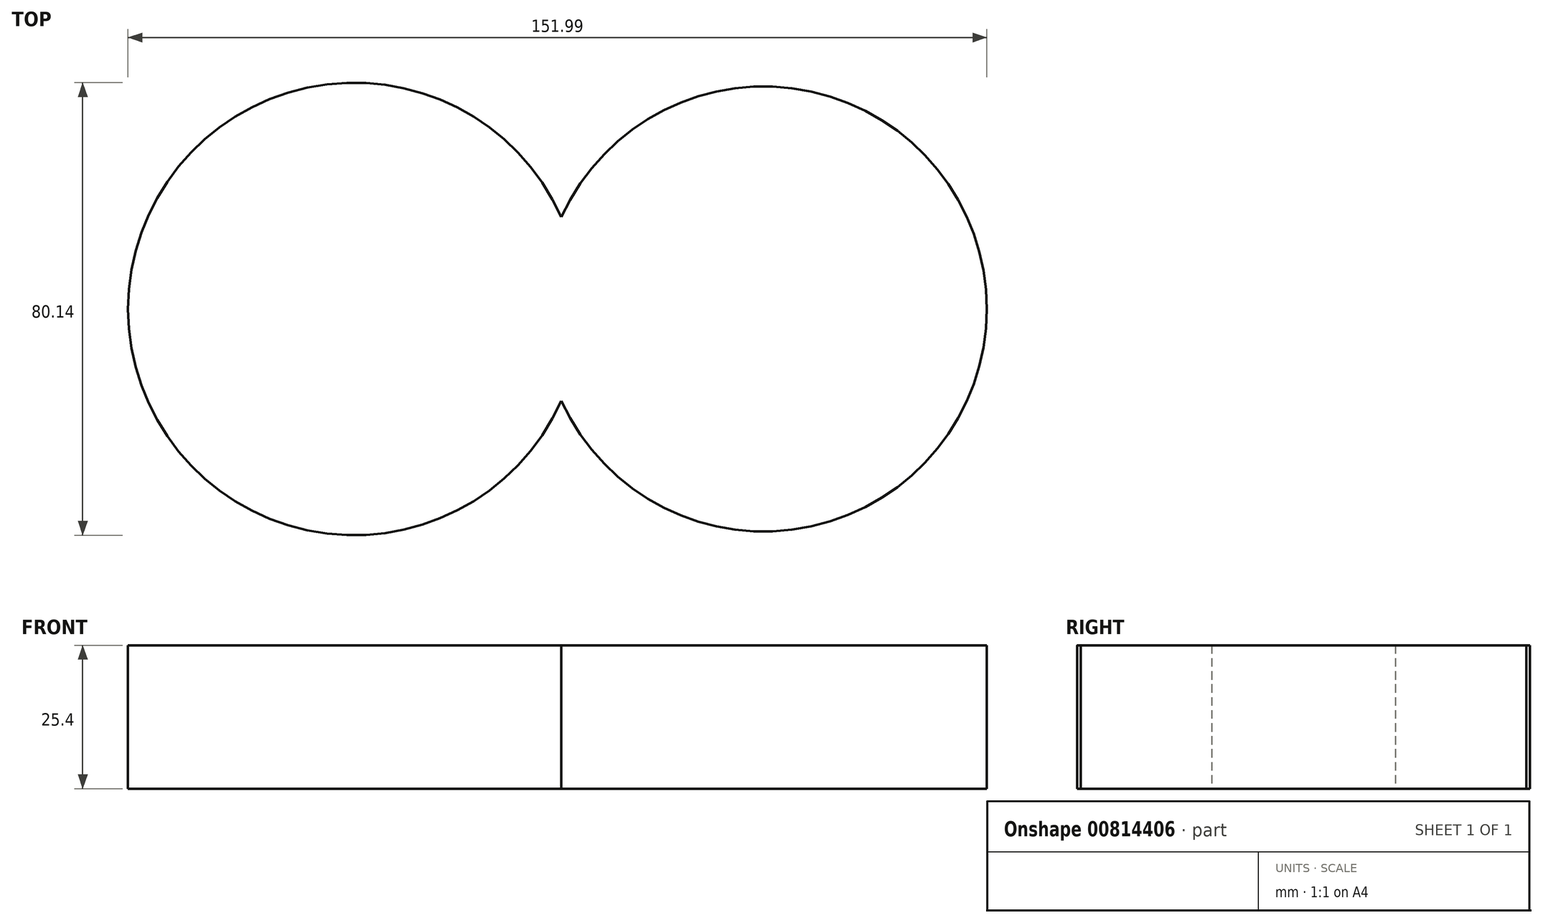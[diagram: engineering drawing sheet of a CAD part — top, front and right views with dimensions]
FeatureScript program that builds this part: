
annotation { "Feature Type Name" : "Feature", "Feature Type Description" : "" }
export const myFeature = defineFeature(function(context is Context, id is Id, definition is map)
    precondition{}
    {
        {
            var Q0;
            Q0=qCreatedBy(makeId("Top.planeOp"),FACE);
            var sketch = newSketch(context, id + "F0", { "sketchPlane" : qUnion([Q0])});
            skArc(sketch, "E0", {"start": v(0, 0) * mm, "mid": v(75.31, 16.26) * mm, "end": v(0, 32.52) * mm});
            skArc(sketch, "E1", {"start": v(0, 32.52) * mm, "mid": v(-76.68, 16.26) * mm, "end": v(0, 0) * mm});
            skSolve(sketch);
        }
        {
            var Q0;
            Q0=makeQuery(id+"F0.imprint","IMPRINT",FACE,{"disambiguationData":[TD([[makeQuery(id+"F0.imprint","IMPRINT",EDGE,{"derivedFrom":sQuery(id+"F0.wireOp",EDGE,"E0")}),1.0]])]});
            extrude(context, id + "F1", {"entities" : qUnion([Q0]), "depth" : 25.4 * mm, "offsetDistance" : 25.4 * mm});
        }
    });
